# Revit family: batten_41-n_51lp327km20an
name_source: partatom
category: Lighting Fixtures
units: mm (PartAtom-declared; Revit-internal decimal feet)

## family parameters
Cut with Voids When Loaded = No
Host = Face
Light Source = No
Part Type = Normal
Room Calculation Point = No
Round Connector Dimension = Use Diameter
Shared = No

## types (1)
- --- (1 x LED, 2000 lm, 16 W, 5000K)
    Apparent Load = 16 VA
    CIE Flux Codes = 37 66 87 87 100
    Color Rendering = 80
    Color Temperature = 5000K
    Default Elevation = 1800 mm
    Description = Batten 41-N, batten luminaire, primary optical cover: cover, of PC, frosted, light emission: direct distribution, primary light characteristic: symmetric, installation type: surface-mounted, LED, rated luminous flux: 2.000lm, luminous efficacy: 125lm/W, light colour: 830/840/850, colour temperature: 3000/4000/5000K, control gear: ON/OFF, with cable with plug, mains connection: 220..240V, AC, 50/60Hz, rated input power: 16W, housing, of aluminium, silver, length: 1.210mm, width: 25mm, height: 44mm, end cap, of PC, white, protection rating (complete): IP20, insulation class (complete): insulation class II (safety insulation), certification: CE, permissible operating ambient temperature: -20..+40°C, packaging unit: 1 piece
    Height = 44 mm
    Lamp = 1 x LED
    Lamp Light Flux = 2000 lm
    Lamp Power = 16 W
    Lamp count = 1
    Length = 1210 mm
    Luminous efficacy = 125 lm/W
    Manufacturer = Siteco
    ModVariant = No
    Model = 51LP327KM20AN
    Mounting Place = Ceiling
    Mounting Type = Surface mounted
    Number of Poles = 1
    OnlyDefault = Yes
    Power Factor = 1
    Product Name = Batten 41-N
    Product group = batten luminaire
    ProductGroupID = 303
    Protection Class = Protection class II
    Protection Degree = IP 20
    RLX_Detail_Level = 1
    RLX_Emergency_Light_Flux = 0 lm
    RLX_Emergency_Type = 0
    RLX_Emergency_Type_DB = No
    RlxData = <blob elided: 43161 chars, md5=1353de9d>
    Socket = socket
    Standby Power = 0 W
    System Light Flux = 2000 lm
    System Power = 16 W
    Type Comments = individual setting: colour temperature 5000K
    Type Image = l_1007254.jpg
    URL = http://relux.com
    VarID = @adj_022786
    Voltage = 0 V
    Weight = 0.00 kg
    Width = 25 mm  [stored 0.082021 ft]

note: [stored X ft] marks values corroborated as IEEE doubles in the binary element streams (Revit-internal decimal feet)

## geometry (parser evidence)
native form markers: Sweep x11
no freeform markers — native parametric forms only
